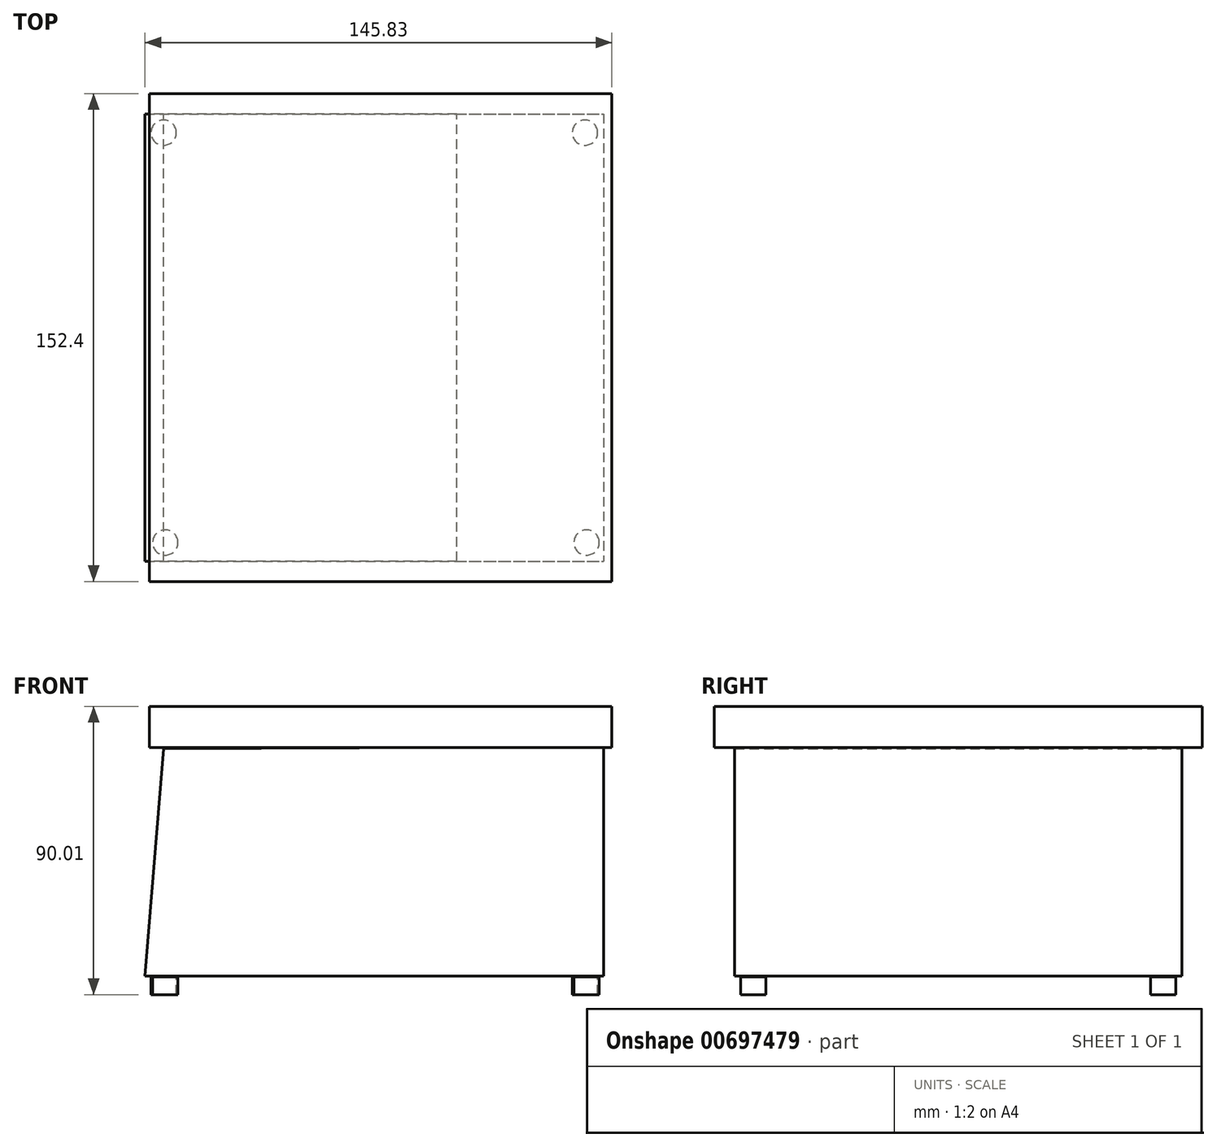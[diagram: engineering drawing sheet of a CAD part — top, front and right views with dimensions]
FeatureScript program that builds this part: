
annotation { "Feature Type Name" : "Feature", "Feature Type Description" : "" }
export const myFeature = defineFeature(function(context is Context, id is Id, definition is map)
    precondition{}
    {
        {
            var Q0;
            Q0=qCreatedBy(makeId("Front.planeOp"),FACE);
            var sketch = newSketch(context, id + "F0", { "sketchPlane" : qUnion([Q0])});
            skLineSegment(sketch, "E0.bottom", {"start": v(-72.22, 56.87) * mm, "end": v(72.22, 56.87) * mm});
            skLineSegment(sketch, "E0.top", {"start": v(-72.22, 44.08) * mm, "end": v(72.22, 44.08) * mm});
            skLineSegment(sketch, "E0.left", {"start": v(-72.22, 56.87) * mm, "end": v(-72.22, 44.08) * mm});
            skLineSegment(sketch, "E0.right", {"start": v(72.22, 56.87) * mm, "end": v(72.22, 44.08) * mm});
            skLineSegment(sketch, "E1", {"start": v(-60.5, 44.08) * mm, "end": v(-74.03, -18.96) * mm});
            skLineSegment(sketch, "E2", {"start": v(-74.03, -18.96) * mm, "end": v(70.13, -18.96) * mm});
            skLineSegment(sketch, "E3", {"start": v(70.13, -18.96) * mm, "end": v(70.13, 44.08) * mm});
            skLineSegment(sketch, "E4", {"start": v(-65.47, -13.14) * mm, "end": v(-65.47, -31.52) * mm});
            skLineSegment(sketch, "E5.bottom", {"start": v(-71.99, -18.96) * mm, "end": v(-58.73, -18.96) * mm});
            skLineSegment(sketch, "E5.top", {"start": v(-71.99, -26.17) * mm, "end": v(-58.73, -26.17) * mm});
            skLineSegment(sketch, "E5.left", {"start": v(-71.99, -18.96) * mm, "end": v(-71.99, -26.17) * mm});
            skLineSegment(sketch, "E5.right", {"start": v(-58.73, -18.96) * mm, "end": v(-58.73, -26.17) * mm});
            skSolve(sketch);
        }
        {
            var Q0;
            Q0=makeQuery(id+"F0.imprint","IMPRINT",FACE,{"disambiguationData":[TD([[makeQuery(id+"F0.imprint","IMPRINT",EDGE,{"derivedFrom":sQuery(id+"F0.wireOp",EDGE,"E0.bottom")}),-1.0]])]});
            extrude(context, id + "F1", {"entities" : qUnion([Q0]), "endBound" : BoundingType.SYMMETRIC, "depth" : 152.4 * mm, "offsetDistance" : 25.4 * mm});
        }
        {
            var Q0;
            Q0=qCreatedBy(makeId("Front.planeOp"),FACE);
            var sketch = newSketch(context, id + "F2", { "sketchPlane" : qUnion([Q0])});
            skLineSegment(sketch, "E6", {"start": v(-67.8, 43.61) * mm, "end": v(-73.61, -27.33) * mm});
            skLineSegment(sketch, "E7", {"start": v(-73.61, -27.33) * mm, "end": v(69.66, -27.33) * mm});
            skLineSegment(sketch, "E8", {"start": v(69.66, -27.33) * mm, "end": v(69.66, 44.3) * mm});
            skLineSegment(sketch, "E9", {"start": v(69.66, 44.3) * mm, "end": v(-67.8, 43.61) * mm});
            skSolve(sketch);
        }
        {
            var Q0;
            Q0=makeQuery(id+"F2.imprint","IMPRINT",FACE,{"disambiguationData":[TD([[makeQuery(id+"F2.imprint","IMPRINT",EDGE,{"derivedFrom":sQuery(id+"F2.wireOp",EDGE,"E6")}),1.0]])]});
            extrude(context, id + "F3", {"entities" : qUnion([Q0]), "operationType" : NewBodyOperationType.ADD, "endBound" : BoundingType.SYMMETRIC, "depth" : 139.7 * mm, "offsetDistance" : 25.4 * mm});
        }
        {
            var Q0;
            Q0=qCreatedBy(makeId("Front.planeOp"),FACE);
            var sketch = newSketch(context, id + "F4", { "sketchPlane" : qUnion([Q0])});
            skLineSegment(sketch, "E10", {"start": v(-65.24, -22.21) * mm, "end": v(-65.24, -37.1) * mm});
            skLineSegment(sketch, "E11.bottom", {"start": v(-69.2, -27.56) * mm, "end": v(-65.24, -27.56) * mm});
            skLineSegment(sketch, "E11.top", {"start": v(-69.2, -33.14) * mm, "end": v(-65.24, -33.14) * mm});
            skLineSegment(sketch, "E11.left", {"start": v(-69.2, -27.56) * mm, "end": v(-69.2, -33.14) * mm});
            skLineSegment(sketch, "E11.right", {"start": v(-65.24, -27.56) * mm, "end": v(-65.24, -33.14) * mm});
            skSolve(sketch);
        }
        {
            var Q0;
            Q0=makeQuery(id+"F4.imprint","IMPRINT",FACE,{"disambiguationData":[TD([[makeQuery(id+"F4.imprint","IMPRINT",EDGE,{"derivedFrom":sQuery(id+"F4.wireOp",EDGE,"E11.bottom")}),-1.0]])]});
            var Q1;
            Q1=sQuery(id+"F4.wireOp",EDGE,"E10");
            revolve(context, id + "F5", {"entities" : qUnion([Q0]), "axis" : qUnion([Q1]), "revolveType" : RevolveType.FULL});
        }
        {
            var Q0;
            Q0=makeQuery(id+"F5.opRevolve","SWEPT_BODY",BODY,{"disambiguationData":[OSD([sQuery(id+"F4.wireOp",EDGE,"E11.bottom"),sQuery(id+"F4.wireOp",EDGE,"E11.top"),sQuery(id+"F4.wireOp",EDGE,"E11.left"),sQuery(id+"F4.wireOp",EDGE,"E11.right")])]});
            transform(context, id + "F6", {"entities" : qUnion([Q0]), "transformType" : TransformType.TRANSLATION_3D, "dx" : -2.03 * mm, "dy" : -64 * mm, "dz" : 0 * mm, "makeCopy" : true});
        }
        {
            var Q0;
            Q0=makeQuery(id+"F5.opRevolve","SWEPT_BODY",BODY,{"disambiguationData":[OSD([sQuery(id+"F4.wireOp",EDGE,"E11.bottom"),sQuery(id+"F4.wireOp",EDGE,"E11.top"),sQuery(id+"F4.wireOp",EDGE,"E11.left"),sQuery(id+"F4.wireOp",EDGE,"E11.right")])]});
            transform(context, id + "F7", {"entities" : qUnion([Q0]), "transformType" : TransformType.TRANSLATION_3D, "dx" : -2.54 * mm, "dy" : 64 * mm, "dz" : 0 * mm, "makeCopy" : false});
        }
        {
            var Q0;
            Q0=makeQuery(id+"F5.opRevolve","SWEPT_BODY",BODY,{"disambiguationData":[OSD([sQuery(id+"F4.wireOp",EDGE,"E11.bottom"),sQuery(id+"F4.wireOp",EDGE,"E11.top"),sQuery(id+"F4.wireOp",EDGE,"E11.left"),sQuery(id+"F4.wireOp",EDGE,"E11.right")])]});
            transform(context, id + "F8", {"entities" : qUnion([Q0]), "transformType" : TransformType.TRANSLATION_3D, "dx" : 131.57 * mm, "dy" : 0 * mm, "dz" : 0 * mm, "makeCopy" : true});
        }
        {
            var Q0;
            Q0=makeQuery(id+"F6.opPattern","COPY",BODY,{"derivedFrom":makeQuery(id+"F5.opRevolve","SWEPT_BODY",BODY,{"disambiguationData":[OSD([sQuery(id+"F4.wireOp",EDGE,"E11.bottom"),sQuery(id+"F4.wireOp",EDGE,"E11.top"),sQuery(id+"F4.wireOp",EDGE,"E11.left"),sQuery(id+"F4.wireOp",EDGE,"E11.right")])]}),"instanceName":"1"});
            transform(context, id + "F9", {"entities" : qUnion([Q0]), "transformType" : TransformType.TRANSLATION_3D, "dx" : 131.57 * mm, "dy" : 0 * mm, "dz" : 0 * mm, "makeCopy" : true});
        }
    });
